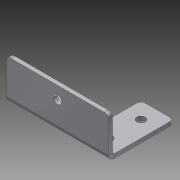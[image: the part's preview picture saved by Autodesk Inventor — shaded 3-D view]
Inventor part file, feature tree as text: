
AUTODESK INVENTOR PART (.ipt)
format: ipt  version: 2013 (Build 170138000, 138)  size: 222,208 bytes
history: native  units: in
note: dims shown in document units (in); Inventor stores cm internally (conversion verified against a paired STEP export)
features: sheet_metal_op x4, other x4, sketch x3, chamfer x1
ambient origin geometry x8: Origin, YZ Plane, XZ Plane, XY Plane, X Axis, Y Axis, Z Axis, Center Point
feature tree (12):
  sheet_metal_op  "Face1"
  sheet_metal_op  "Flange1"
  chamfer  "Corner Round1"
  sketch  "Sketch1"  dims[d0=2.0in]
  other  "Plate1"
  sketch  "Sketch2"  dims[d1=1.0in]
  other  "Plate2"
  sheet_metal_op  "Bend1"
  sheet_metal_op  "Corner1"
  sketch  "Sketch3"  dims[d2=0.26in d3=0.26in d4=1.0in d8=0.125in d9=0.125in d10=0.0625in d11=0.25in d12=0.125in d13=1.25in d14=90.0deg d15=0.05in d16=0.5in d17=0.125in d18=0.125in d19=0.26in d22=0.125in d23=0.0in d24=0.125in d25=2.125in d26=2.25in d27=0.75in d28=0.875in d29=2.25in d5=0.125in d6=0.0in]
  other  "Cut1"
  other  "Definition1"
